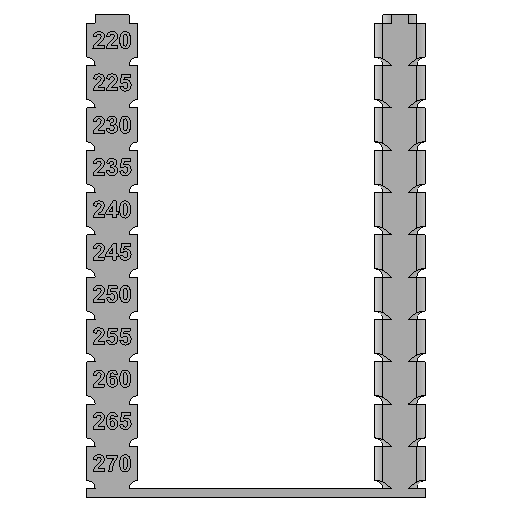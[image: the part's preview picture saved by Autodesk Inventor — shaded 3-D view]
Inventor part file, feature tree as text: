
AUTODESK INVENTOR PART (.ipt)
format: ipt  version: 2025.3 (Build 293356000, 356)  size: 1,726,976 bytes
history: native  units: mm
features: other x8, extrude x4, sketch x2, mirror x2, fillet x2, pattern_linear x2
ambient origin geometry x8: Origin, YZ Plane, XZ Plane, XY Plane, X Axis, Y Axis, Z Axis, Center Point
bodies: Body1 (feature_tree)
feature tree (20):
  other  "實體1"
  other  "temp_tower"
  sketch  "草圖1"
  extrude  "擠出1"  Depth=40.0mm
  extrude  "擠出2"  Depth=5.0mm
  mirror  "鏡射1"
  extrude  "擠出3"  Depth=6.0mm
  extrude  "擠出4"  Depth=1.0mm
  mirror  "鏡射2"
  fillet  "圓角1"  Radius=1.0mm
  pattern_linear  "矩形陣列1"  Spacing1=4.0mm  [1 undecoded]
  other  "合併1"
  fillet  "圓角2"  Radius=1.0mm
  pattern_linear  "矩形陣列2"  Spacing1=1.0mm  [1 undecoded]
  other  "浮雕1"
  other  "實體2"
  other  "陣列 實體2:1"
  other  "實體3"
  sketch  "草圖2"
  other  "MeshFeature1"
note: 2 required parameter values undecoded (feature->parameter linkage not recoverable at this tier; creation-order binding heuristic only, values carry confidence <= 0.55)
